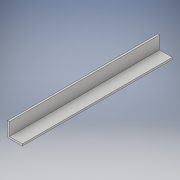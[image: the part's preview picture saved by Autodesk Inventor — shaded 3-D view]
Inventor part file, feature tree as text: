
AUTODESK INVENTOR PART (.ipt)
format: ipt  version: 2017 (Build 210142000, 142)  size: 97,280 bytes
history: native  units: in
note: dims shown in document units (in); Inventor stores cm internally (conversion verified against a paired STEP export)
features: extrude x1, sketch x1
ambient origin geometry x8: Origin, YZ Plane, XZ Plane, XY Plane, X Axis, Y Axis, Z Axis, Center Point
bodies: Solid1 (feature_tree)
feature tree (2):
  extrude  "Extrusion1"  Depth=1.0in
  sketch  "Sketch1"  dims[d4=10.188in d5=0.0in d6=1.0in d7=1.0in]
